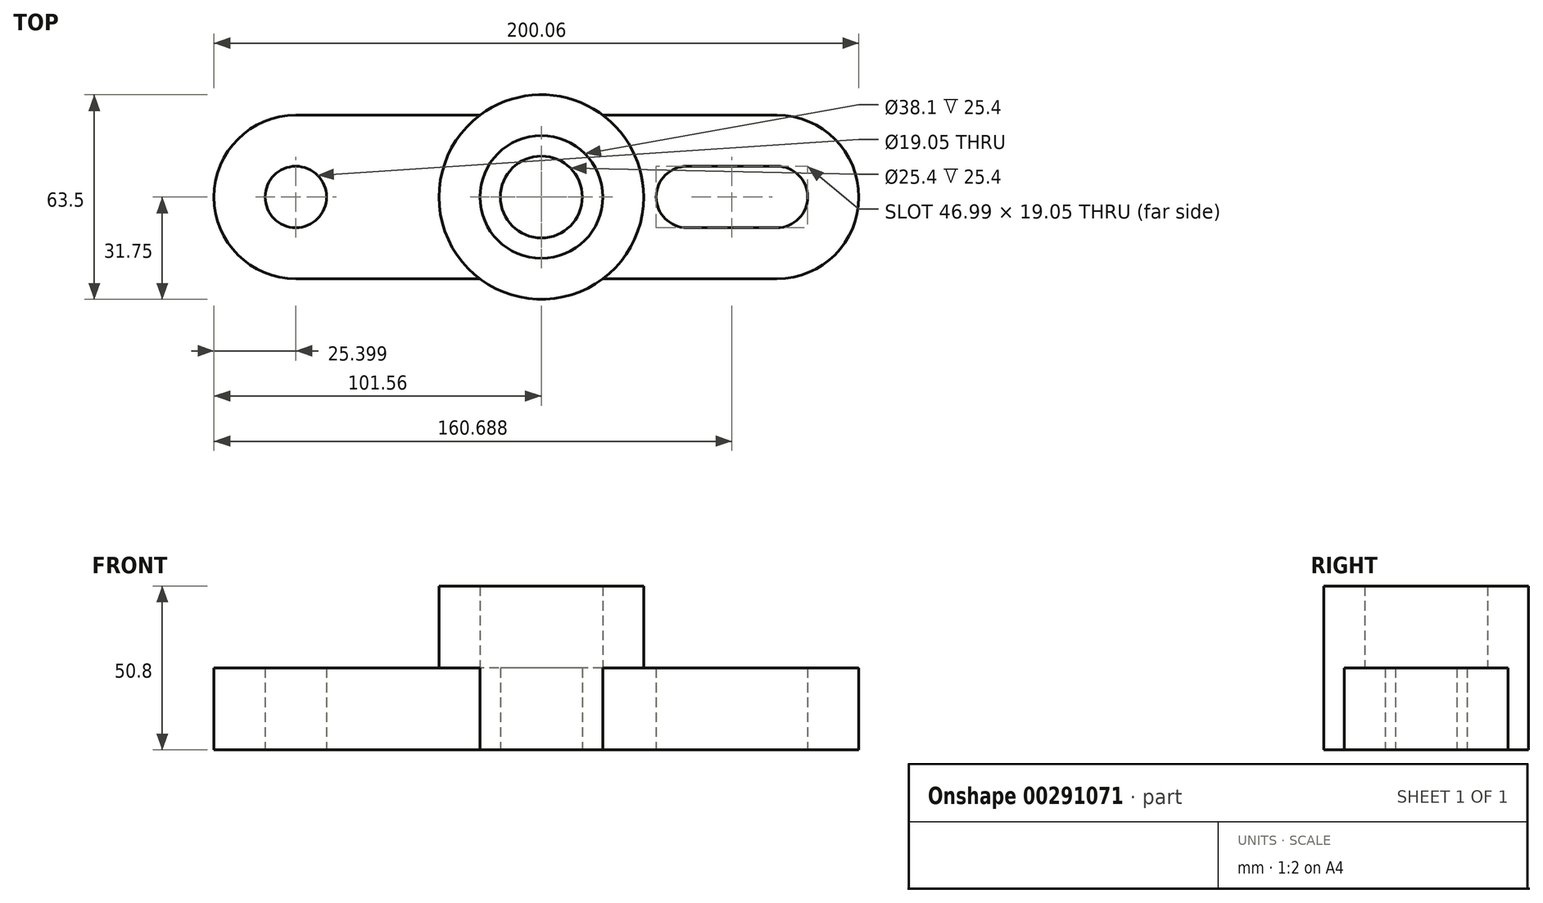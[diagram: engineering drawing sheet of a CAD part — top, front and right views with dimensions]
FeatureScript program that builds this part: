
annotation { "Feature Type Name" : "Feature", "Feature Type Description" : "" }
export const myFeature = defineFeature(function(context is Context, id is Id, definition is map)
    precondition{}
    {
        {
            var Q0;
            Q0=qCreatedBy(makeId("Top.planeOp"),FACE);
            var sketch = newSketch(context, id + "F0", { "sketchPlane" : qUnion([Q0])});
            skCircle(sketch, "E0", {"center": v(0, 0) * mm, "radius": 12.7 * mm});
            skCircle(sketch, "E1", {"center": v(0, 0) * mm, "radius": 19.05 * mm});
            skCircle(sketch, "E2", {"center": v(0, 0) * mm, "radius": 31.75 * mm});
            skLineSegment(sketch, "E3", {"start": v(19.05, -25.4) * mm, "end": v(73.1, -25.4) * mm});
            skLineSegment(sketch, "E4", {"start": v(-19.05, -25.4) * mm, "end": v(-76.33, -25.4) * mm});
            skLineSegment(sketch, "E5", {"start": v(19.05, 25.4) * mm, "end": v(73.1, 25.4) * mm});
            skLineSegment(sketch, "E6", {"start": v(-19.05, 25.4) * mm, "end": v(-76.33, 25.4) * mm});
            skArc(sketch, "E7", {"start": v(-76.16, 25.4) * mm, "mid": v(-101.56, 0) * mm, "end": v(-76.16, -25.4) * mm});
            skArc(sketch, "E8", {"start": v(73.1, -25.4) * mm, "mid": v(98.5, 0) * mm, "end": v(73.1, 25.4) * mm});
            skCircle(sketch, "E9", {"center": v(-76.16, 0) * mm, "radius": 9.53 * mm});
            skArc(sketch, "E10", {"start": v(73.1, -9.52) * mm, "mid": v(82.62, 0) * mm, "end": v(73.1, 9.53) * mm});
            skArc(sketch, "E11", {"start": v(45.16, 9.53) * mm, "mid": v(35.63, 0) * mm, "end": v(45.16, -9.53) * mm});
            skLineSegment(sketch, "E12", {"start": v(73.1, -9.52) * mm, "end": v(45.16, -9.53) * mm});
            skLineSegment(sketch, "E13", {"start": v(45.16, 9.52) * mm, "end": v(73.1, 9.52) * mm});
            skSolve(sketch);
        }
        {
            var Q0;
            Q0=makeQuery(id+"F0.imprint","IMPRINT",FACE,{"disambiguationData":[TD([[makeQuery(id+"F0.imprint","IMPRINT",EDGE,{"derivedFrom":sQuery(id+"F0.wireOp",EDGE,"E1")}),-1.0]])]});
            extrude(context, id + "F1", {"entities" : qUnion([Q0]), "depth" : 50.8 * mm});
        }
        {
            var Q0;
            {var subQ0=sQuery(id+"F0.wireOp",EDGE,"E7");Q0=makeQuery(id+"F0.imprint","IMPRINT",FACE,{"disambiguationData":[TD([[makeQuery(id+"F0.imprint","IMPRINT",EDGE,{"derivedFrom":subQ0}),1.0]])]});}
            extrude(context, id + "F2", {"entities" : qUnion([Q0]), "operationType" : NewBodyOperationType.ADD, "depth" : 25.4 * mm});
        }
        {
            var Q0;
            {var subQ1=sQuery(id+"F0.wireOp",EDGE,"E3");Q0=makeQuery(id+"F0.imprint","IMPRINT",FACE,{"disambiguationData":[TD([[makeQuery(id+"F0.imprint","IMPRINT",EDGE,{"derivedFrom":subQ1}),1.0]])]});}
            extrude(context, id + "F3", {"entities" : qUnion([Q0]), "operationType" : NewBodyOperationType.ADD, "depth" : 25.4 * mm});
        }
        {
            var Q0;
            Q0=makeQuery(id+"F0.imprint","IMPRINT",FACE,{"disambiguationData":[TD([[makeQuery(id+"F0.imprint","IMPRINT",EDGE,{"derivedFrom":sQuery(id+"F0.wireOp",EDGE,"E0")}),-1.0]])]});
            extrude(context, id + "F4", {"entities" : qUnion([Q0]), "operationType" : NewBodyOperationType.ADD, "depth" : 25.4 * mm});
        }
    });
